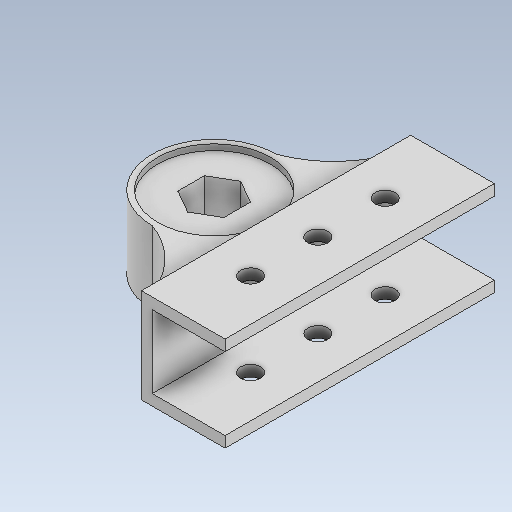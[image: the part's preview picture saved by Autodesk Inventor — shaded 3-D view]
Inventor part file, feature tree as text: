
AUTODESK INVENTOR PART (.ipt)
format: ipt  version: 2023 (Build 270158000, 158)  size: 329,728 bytes
history: native  units: in
note: dims shown in document units (in); Inventor stores cm internally (conversion verified against a paired STEP export)
features: sketch x11, extrude x9, hole x2
ambient origin geometry x8: Origin, YZ Plane, XZ Plane, XY Plane, X Axis, Y Axis, Z Axis, Center Point
bodies: Solid1 (feature_tree)
feature tree (22):
  extrude  "Extrusion1"  Depth=0.7866in TaperAngle=0.0deg
  extrude  "Extrusion2"  Depth=0.0634in TaperAngle=0.0deg
  extrude  "Extrusion4"  Depth=0.0634in TaperAngle=0.0deg
  extrude  "Extrusion5"  Depth=0.7874in
  extrude  "Extrusion6"  Depth=0.7866in TaperAngle=0.0deg
  extrude  "Extrusion7"  Depth=0.1181in TaperAngle=0.0deg
  extrude  "Extrusion8"  Depth=0.1181in
  extrude  "Extrusion9"  Depth=0.1181in
  extrude  "Extrusion10"  TaperAngle=0.0deg  [1 undecoded]
  hole  "Hole1"  [1 undecoded]
  hole  "Hole2"  [1 undecoded]
  sketch  "Sketch1"  dims[d6=1.3386in d7=0.7866in d8=0.0in]
  sketch  "Sketch2"  dims[d9=1.2205in d10=0.0634in d11=0.0in]
  sketch  "Sketch4"  dims[d15=1.2205in d16=0.0634in d17=0.0in]
  sketch  "Sketch5"  dims[d18=0.7874in d19=0.7874in]
  sketch  "Sketch7"  dims[d20=0.7874in d21=0.7866in d22=0.0in]
  sketch  "Sketch9"  dims[d23=0.1181in d24=0.0in d25=0.1181in d26=0.0in]
  sketch  "Sketch11"  dims[d27=0.1181in d28=0.0in d29=0.1181in]
  sketch  "Sketch12"  dims[d30=0.1181in d31=0.1181in]
  sketch  "Sketch13"  dims[d32=0.0in d33=0.0in d35=0.0in d36=0.0in]
  sketch  "Sketch14"  dims[d37=0.4528in d38=1.4567in]
  sketch  "Sketch15"  dims[d39=0.2165in d40=0.2362in d41=0.4094in d42=0.0787in d43=90.0deg d44=0.315in d45=0.8108in d47=0.7283in d48=0.7283in d49=0.2165in d50=0.2362in d51=0.1575in d52=0.0787in d53=90.0deg d54=0.315in d55=0.8108in]
note: 3 required parameter values undecoded (feature->parameter linkage not recoverable at this tier; creation-order binding heuristic only, values carry confidence <= 0.55)
